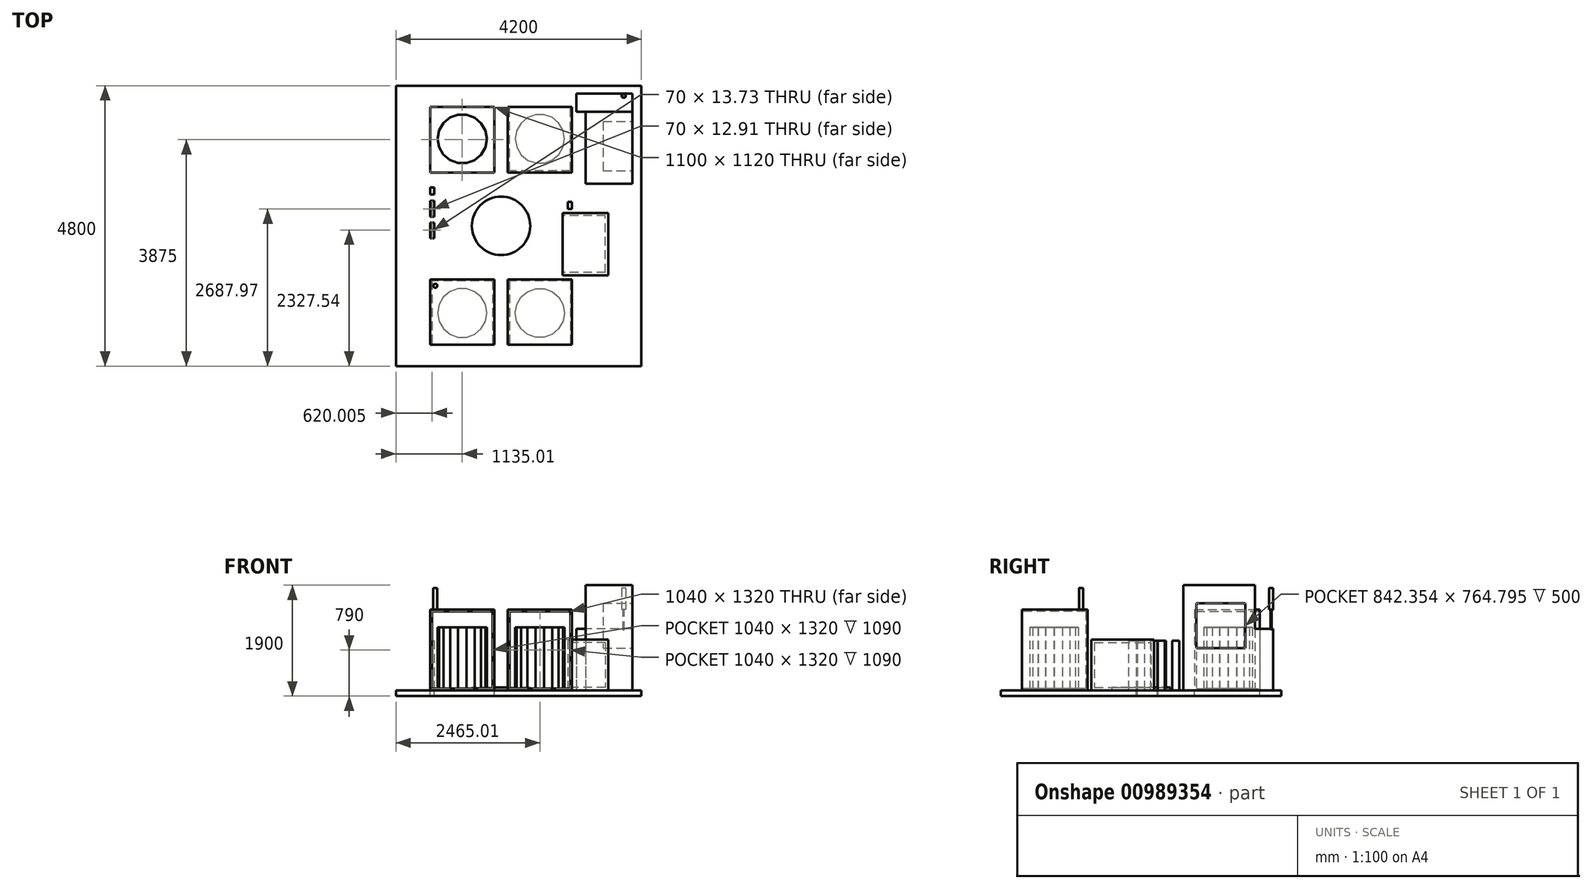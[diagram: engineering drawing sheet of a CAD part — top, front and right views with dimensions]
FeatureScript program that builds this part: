
annotation { "Feature Type Name" : "Feature", "Feature Type Description" : "" }
export const myFeature = defineFeature(function(context is Context, id is Id, definition is map)
    precondition{}
    {
        {
            var Q0;
            Q0=qCreatedBy(makeId("Top.planeOp"),FACE);
            var sketch = newSketch(context, id + "F0", { "sketchPlane" : qUnion([Q0])});
            skLineSegment(sketch, "E0.bottom", {"start": v(-4186.95, 4400.9) * mm, "end": v(13.05, 4400.9) * mm});
            skLineSegment(sketch, "E0.top", {"start": v(-4186.95, -399.1) * mm, "end": v(13.05, -399.1) * mm});
            skLineSegment(sketch, "E0.left", {"start": v(-4186.95, 4400.9) * mm, "end": v(-4186.95, -399.1) * mm});
            skLineSegment(sketch, "E0.right", {"start": v(13.05, 4400.9) * mm, "end": v(13.05, -399.1) * mm});
            skLineSegment(sketch, "E1", {"start": v(13.05, 2000.9) * mm, "end": v(-2386.95, 2000.9) * mm});
            skCircle(sketch, "E2", {"center": v(-2386.95, 2000.9) * mm, "radius": 500 * mm});
            skLineSegment(sketch, "E3.bottom", {"start": v(-2504.03, 4400.9) * mm, "end": v(-3604.03, 4400.9) * mm});
            skLineSegment(sketch, "E4.bottom", {"start": v(-1092.36, 4400.9) * mm, "end": v(-2192.36, 4400.9) * mm});
            skLineSegment(sketch, "E5.bottom", {"start": v(-550.98, 1154) * mm, "end": v(-1330.98, 1154) * mm});
            skLineSegment(sketch, "E5.top", {"start": v(-550.98, 2224) * mm, "end": v(-1330.98, 2224) * mm});
            skLineSegment(sketch, "E5.left", {"start": v(-550.98, 1154) * mm, "end": v(-550.98, 2224) * mm});
            skLineSegment(sketch, "E5.right", {"start": v(-1330.98, 1154) * mm, "end": v(-1330.98, 2224) * mm});
            skLineSegment(sketch, "E6.bottom", {"start": v(-141.16, 2724.16) * mm, "end": v(-941.16, 2724.16) * mm});
            skLineSegment(sketch, "E6.top", {"start": v(-141.16, 3954.16) * mm, "end": v(-941.16, 3954.16) * mm});
            skLineSegment(sketch, "E6.left", {"start": v(-141.16, 2724.16) * mm, "end": v(-141.16, 3954.16) * mm});
            skLineSegment(sketch, "E6.right", {"start": v(-941.16, 2724.16) * mm, "end": v(-941.16, 3954.16) * mm});
            skLineSegment(sketch, "E7.bottom", {"start": v(-141.16, 3954.16) * mm, "end": v(-1101.16, 3954.16) * mm});
            skLineSegment(sketch, "E7.top", {"start": v(-141.16, 4264.16) * mm, "end": v(-1101.16, 4264.16) * mm});
            skLineSegment(sketch, "E7.left", {"start": v(-141.16, 3954.16) * mm, "end": v(-141.16, 4264.16) * mm});
            skLineSegment(sketch, "E7.right", {"start": v(-1101.16, 3954.16) * mm, "end": v(-1101.16, 4264.16) * mm});
            skLineSegment(sketch, "E8.bottom", {"start": v(-1171.95, 1085.9) * mm, "end": v(-3601.95, 1085.9) * mm});
            skLineSegment(sketch, "E8.top", {"start": v(-1171.95, 2915.9) * mm, "end": v(-3601.95, 2915.9) * mm});
            skLineSegment(sketch, "E8.left", {"start": v(-1171.95, 1085.9) * mm, "end": v(-1171.95, 2915.9) * mm});
            skLineSegment(sketch, "E8.right", {"start": v(-3601.95, 1085.9) * mm, "end": v(-3601.95, 2915.9) * mm});
            skLineSegment(sketch, "E9.bottom", {"start": v(-1171.95, 2915.9) * mm, "end": v(-2271.95, 2915.9) * mm});
            skLineSegment(sketch, "E9.top", {"start": v(-1171.95, 4035.9) * mm, "end": v(-2271.95, 4035.9) * mm});
            skLineSegment(sketch, "E9.left", {"start": v(-1171.95, 2915.9) * mm, "end": v(-1171.95, 4035.9) * mm});
            skLineSegment(sketch, "E9.right", {"start": v(-2271.95, 2915.9) * mm, "end": v(-2271.95, 4035.9) * mm});
            skLineSegment(sketch, "E10.bottom", {"start": v(-3601.95, 2915.9) * mm, "end": v(-2501.95, 2915.9) * mm});
            skLineSegment(sketch, "E10.top", {"start": v(-3601.95, 4035.9) * mm, "end": v(-2501.95, 4035.9) * mm});
            skLineSegment(sketch, "E10.left", {"start": v(-3601.95, 2915.9) * mm, "end": v(-3601.95, 4035.9) * mm});
            skLineSegment(sketch, "E10.right", {"start": v(-2501.95, 2915.9) * mm, "end": v(-2501.95, 4035.9) * mm});
            skLineSegment(sketch, "E11.MirrorCS", {"start": v(-1171.95, 1085.9) * mm, "end": v(-1171.95, -34.1) * mm});
            skLineSegment(sketch, "E12.MirrorCS", {"start": v(-1171.95, -34.1) * mm, "end": v(-2271.95, -34.1) * mm});
            skLineSegment(sketch, "E13.MirrorCS", {"start": v(-2271.95, 1085.9) * mm, "end": v(-2271.95, -34.1) * mm});
            skLineSegment(sketch, "E14.MirrorCS", {"start": v(-2501.95, 1085.9) * mm, "end": v(-2501.95, -34.1) * mm});
            skLineSegment(sketch, "E15.MirrorCS", {"start": v(-3601.95, -34.1) * mm, "end": v(-2501.95, -34.1) * mm});
            skLineSegment(sketch, "E16.MirrorCS", {"start": v(-3601.95, 1085.9) * mm, "end": v(-3601.95, -34.1) * mm});
            skLineSegment(sketch, "E17.bottom", {"start": v(-1171.95, 2408.86) * mm, "end": v(-1241.95, 2408.86) * mm});
            skLineSegment(sketch, "E17.top", {"start": v(-1171.95, 2288.86) * mm, "end": v(-1241.95, 2288.86) * mm});
            skLineSegment(sketch, "E17.left", {"start": v(-1171.95, 2408.86) * mm, "end": v(-1171.95, 2288.86) * mm});
            skLineSegment(sketch, "E17.right", {"start": v(-1241.95, 2408.86) * mm, "end": v(-1241.95, 2288.86) * mm});
            skLineSegment(sketch, "E18.left", {"start": v(-3601.95, 2000.9) * mm, "end": v(-3601.95, 2383.24) * mm});
            skLineSegment(sketch, "E19.bottom", {"start": v(-3601.95, 1786.57) * mm, "end": v(-3531.95, 1786.57) * mm});
            skLineSegment(sketch, "E19.top", {"start": v(-3601.95, 2056.57) * mm, "end": v(-3531.95, 2056.57) * mm});
            skLineSegment(sketch, "E19.left", {"start": v(-3601.95, 1786.57) * mm, "end": v(-3601.95, 2056.57) * mm});
            skLineSegment(sketch, "E19.right", {"start": v(-3531.95, 1786.57) * mm, "end": v(-3531.95, 2056.57) * mm});
            skLineSegment(sketch, "E20.bottom", {"start": v(-3601.95, 2160.32) * mm, "end": v(-3531.95, 2160.32) * mm});
            skLineSegment(sketch, "E20.top", {"start": v(-3601.95, 2430.32) * mm, "end": v(-3531.95, 2430.32) * mm});
            skLineSegment(sketch, "E20.left", {"start": v(-3601.95, 2160.32) * mm, "end": v(-3601.95, 2430.32) * mm});
            skLineSegment(sketch, "E20.right", {"start": v(-3531.95, 2160.32) * mm, "end": v(-3531.95, 2430.32) * mm});
            skLineSegment(sketch, "E21.bottom", {"start": v(-3601.95, 2538.18) * mm, "end": v(-3531.95, 2538.18) * mm});
            skLineSegment(sketch, "E21.top", {"start": v(-3601.95, 2658.18) * mm, "end": v(-3531.95, 2658.18) * mm});
            skLineSegment(sketch, "E21.left", {"start": v(-3601.95, 2538.18) * mm, "end": v(-3601.95, 2658.18) * mm});
            skLineSegment(sketch, "E21.right", {"start": v(-3531.95, 2538.18) * mm, "end": v(-3531.95, 2658.18) * mm});
            skLineSegment(sketch, "E22", {"start": v(-3531.95, 2295.32) * mm, "end": v(-3601.95, 2295.32) * mm});
            skLineSegment(sketch, "E23", {"start": v(-3531.95, 1921.57) * mm, "end": v(-3601.95, 1921.57) * mm});
            skLineSegment(sketch, "E24", {"start": v(-3531.95, 2282.4) * mm, "end": v(-3601.95, 2282.4) * mm});
            skLineSegment(sketch, "E25", {"start": v(-3531.95, 1933.96) * mm, "end": v(-3601.95, 1935.3) * mm});
            skLineSegment(sketch, "E26", {"start": v(-1171.95, 2915.9) * mm, "end": v(-2386.95, 2915.9) * mm});
            skLineSegment(sketch, "E27", {"start": v(-2386.95, 2915.9) * mm, "end": v(-2386.95, 4048.28) * mm});
            skSolve(sketch);
        }
        {
            var Q0;
            Q0=makeQuery(id+"F0.imprint","IMPRINT",FACE,{"disambiguationData":[TD([[makeQuery(id+"F0.imprint","IMPRINT",EDGE,{"derivedFrom":sQuery(id+"F0.wireOp",EDGE,"E9.bottom")}),-1.0]])]});
            var Q1;
            Q1=makeQuery(id+"F0.imprint","IMPRINT",FACE,{"disambiguationData":[TD([[makeQuery(id+"F0.imprint","IMPRINT",EDGE,{"derivedFrom":sQuery(id+"F0.wireOp",EDGE,"E10.bottom")}),1.0]])]});
            var Q2;
            {var subQ0=sQuery(id+"F0.wireOp",EDGE,"E11.MirrorCS");Q2=makeQuery(id+"F0.imprint","IMPRINT",FACE,{"disambiguationData":[TD([[makeQuery(id+"F0.imprint","IMPRINT",EDGE,{"derivedFrom":subQ0}),-1.0]])]});}
            var Q3;
            {var subQ2=sQuery(id+"F0.wireOp",EDGE,"E14.MirrorCS");Q3=makeQuery(id+"F0.imprint","IMPRINT",FACE,{"disambiguationData":[TD([[makeQuery(id+"F0.imprint","IMPRINT",EDGE,{"derivedFrom":subQ2}),-1.0]])]});}
            var Q4;
            Q4=makeQuery(id+"F0.imprint","IMPRINT",FACE,{"disambiguationData":[TD([[makeQuery(id+"F0.imprint","IMPRINT",EDGE,{"derivedFrom":sQuery(id+"F0.wireOp",EDGE,"E9.top")}),1.0]])]});
            extrude(context, id + "F1", {"entities" : qUnion([Q0, Q1, Q2, Q3, Q4]), "depth" : 1380 * mm, "offsetDistance" : 25 * mm});
        }
        {
            var Q0;
            Q0=makeQuery(id+"F0.imprint","IMPRINT",FACE,{"disambiguationData":[TD([[makeQuery(id+"F0.imprint","IMPRINT",EDGE,{"derivedFrom":sQuery(id+"F0.wireOp",EDGE,"E6.bottom")}),-1.0]])]});
            extrude(context, id + "F2", {"entities" : qUnion([Q0]), "depth" : 1800 * mm, "offsetDistance" : 25 * mm});
        }
        {
            var Q0;
            Q0=makeQuery(id+"F0.imprint","IMPRINT",FACE,{"disambiguationData":[TD([[makeQuery(id+"F0.imprint","IMPRINT",EDGE,{"derivedFrom":sQuery(id+"F0.wireOp",EDGE,"E7.top")}),1.0]])]});
            extrude(context, id + "F3", {"entities" : qUnion([Q0]), "operationType" : NewBodyOperationType.ADD, "depth" : 1050 * mm, "offsetDistance" : 25 * mm});
        }
        {
            var Q0;
            Q0=makeQuery(id+"F0.imprint","IMPRINT",FACE,{"disambiguationData":[TD([[makeQuery(id+"F0.imprint","IMPRINT",EDGE,{"derivedFrom":sQuery(id+"F0.wireOp",EDGE,"E21.bottom")}),1.0]])]});
            var Q1;
            {var subQ1=sQuery(id+"F0.wireOp",EDGE,"E20.top");Q1=makeQuery(id+"F0.imprint","IMPRINT",FACE,{"disambiguationData":[TD([[makeQuery(id+"F0.imprint","IMPRINT",EDGE,{"derivedFrom":subQ1}),-1.0]])]});}
            var Q2;
            {var subQ0=sQuery(id+"F0.wireOp",EDGE,"E20.bottom");Q2=makeQuery(id+"F0.imprint","IMPRINT",FACE,{"disambiguationData":[TD([[makeQuery(id+"F0.imprint","IMPRINT",EDGE,{"derivedFrom":subQ0}),1.0]])]});}
            var Q3;
            {var subQ1=sQuery(id+"F0.wireOp",EDGE,"E19.top");Q3=makeQuery(id+"F0.imprint","IMPRINT",FACE,{"disambiguationData":[TD([[makeQuery(id+"F0.imprint","IMPRINT",EDGE,{"derivedFrom":subQ1}),-1.0]])]});}
            var Q4;
            {var subQ0=sQuery(id+"F0.wireOp",EDGE,"E19.bottom");Q4=makeQuery(id+"F0.imprint","IMPRINT",FACE,{"disambiguationData":[TD([[makeQuery(id+"F0.imprint","IMPRINT",EDGE,{"derivedFrom":subQ0}),1.0]])]});}
            var Q5;
            Q5=makeQuery(id+"F0.imprint","IMPRINT",FACE,{"disambiguationData":[TD([[makeQuery(id+"F0.imprint","IMPRINT",EDGE,{"derivedFrom":sQuery(id+"F0.wireOp",EDGE,"E17.bottom")}),1.0]])]});
            extrude(context, id + "F4", {"entities" : qUnion([Q0, Q1, Q2, Q3, Q4, Q5]), "depth" : 850 * mm, "offsetDistance" : 25 * mm});
        }
        {
            var Q0;
            Q0=makeQuery(id+"F1.opExtrude","SWEPT_FACE",FACE,{"disambiguationData":[OSD([sQuery(id+"F0.wireOp",EDGE,"E12.MirrorCS")])]});
            var Q1;
            Q1=makeQuery(id+"F1.opExtrude","SWEPT_FACE",FACE,{"disambiguationData":[OSD([sQuery(id+"F0.wireOp",EDGE,"E15.MirrorCS")])]});
            var Q2;
            Q2=makeQuery(id+"F1.opExtrude","SWEPT_FACE",FACE,{"disambiguationData":[OSD([sQuery(id+"F0.wireOp",EDGE,"E10.top")])]});
            var Q3;
            Q3=makeQuery(id+"F1.opExtrude","SWEPT_FACE",FACE,{"disambiguationData":[OSD([sQuery(id+"F0.wireOp",EDGE,"E9.top")])]});
            shell(context, id + "F5", {"entities" : qUnion([Q0, Q1, Q2, Q3]), "thickness" : 30 * mm});
        }
        {
            var Q0;
            Q0=makeQuery(id+"F5.opShell","OFFSET_FACE",FACE,{"disambiguationData":[OSD([sQuery(id+"F0.wireOp",EDGE,"E8.bottom"),sQuery(id+"F0.wireOp",EDGE,"E11.MirrorCS"),sQuery(id+"F0.wireOp",EDGE,"E12.MirrorCS"),sQuery(id+"F0.wireOp",EDGE,"E13.MirrorCS")])]});
            var sketch = newSketch(context, id + "F6", { "sketchPlane" : qUnion([Q0])});
            skLineSegment(sketch, "E28.bottom", {"start": v(-2241.95, -34.1) * mm, "end": v(-1201.95, -34.1) * mm});
            skLineSegment(sketch, "E28.top", {"start": v(-2241.95, 1055.9) * mm, "end": v(-1201.95, 1055.9) * mm});
            skLineSegment(sketch, "E28.left", {"start": v(-2241.95, -34.1) * mm, "end": v(-2241.95, 1055.9) * mm});
            skLineSegment(sketch, "E28.right", {"start": v(-1201.95, -34.1) * mm, "end": v(-1201.95, 1055.9) * mm});
            skLineSegment(sketch, "E29", {"start": v(-1721.95, -34.1) * mm, "end": v(-1721.95, 1055.9) * mm});
            skLineSegment(sketch, "E30", {"start": v(-1721.95, 1055.9) * mm, "end": v(-1721.95, 510.9) * mm});
            skLineSegment(sketch, "E31", {"start": v(-1721.95, 510.9) * mm, "end": v(-1201.95, 510.9) * mm});
            skLineSegment(sketch, "E32", {"start": v(-1201.95, 510.9) * mm, "end": v(-2241.95, 510.9) * mm});
            skCircle(sketch, "E33.cCircle", {"center": v(-1721.95, 510.9) * mm, "radius": 415.23 * mm, "construction": true});
            skLineSegment(sketch, "E33.0", {"start": v(-2043.51, 783.6) * mm, "end": v(-1930.85, 877.14) * mm});
            skLineSegment(sketch, "E33.1", {"start": v(-1930.85, 877.14) * mm, "end": v(-1792.99, 926.5) * mm});
            skLineSegment(sketch, "E33.2", {"start": v(-1792.99, 926.5) * mm, "end": v(-1646.56, 925.73) * mm});
            skLineSegment(sketch, "E33.3", {"start": v(-1646.56, 925.73) * mm, "end": v(-1509.22, 874.93) * mm});
            skLineSegment(sketch, "E33.4", {"start": v(-1509.22, 874.93) * mm, "end": v(-1397.54, 780.22) * mm});
            skLineSegment(sketch, "E33.5", {"start": v(-1397.54, 780.22) * mm, "end": v(-1324.99, 653.03) * mm});
            skLineSegment(sketch, "E33.6", {"start": v(-1324.99, 653.03) * mm, "end": v(-1300.32, 508.69) * mm});
            skLineSegment(sketch, "E33.7", {"start": v(-1300.32, 508.69) * mm, "end": v(-1326.5, 364.62) * mm});
            skLineSegment(sketch, "E33.8", {"start": v(-1326.5, 364.62) * mm, "end": v(-1400.38, 238.19) * mm});
            skLineSegment(sketch, "E33.9", {"start": v(-1400.38, 238.19) * mm, "end": v(-1513.04, 144.65) * mm});
            skLineSegment(sketch, "E33.10", {"start": v(-1513.04, 144.65) * mm, "end": v(-1650.9, 95.29) * mm});
            skLineSegment(sketch, "E33.11", {"start": v(-1650.9, 95.29) * mm, "end": v(-1797.33, 96.05) * mm});
            skLineSegment(sketch, "E33.12", {"start": v(-1797.33, 96.05) * mm, "end": v(-1934.67, 146.86) * mm});
            skLineSegment(sketch, "E33.13", {"start": v(-1934.67, 146.86) * mm, "end": v(-2046.35, 241.57) * mm});
            skLineSegment(sketch, "E33.14", {"start": v(-2046.35, 241.57) * mm, "end": v(-2118.9, 368.76) * mm});
            skLineSegment(sketch, "E33.15", {"start": v(-2118.9, 368.76) * mm, "end": v(-2143.57, 513.1) * mm});
            skLineSegment(sketch, "E33.16", {"start": v(-2143.57, 513.1) * mm, "end": v(-2117.4, 657.17) * mm});
            skLineSegment(sketch, "E33.17", {"start": v(-2117.4, 657.17) * mm, "end": v(-2043.51, 783.6) * mm});
            skPoint(sketch, "E33.0.midPoint", {"position": v(-1987.18, 830.37) * mm});
            skLineSegment(sketch, "E34.MirrorCS", {"start": v(-1721.95, 4035.9) * mm, "end": v(-1721.95, 2945.9) * mm});
            skLineSegment(sketch, "E35.MirrorCS", {"start": v(-1201.95, 3490.9) * mm, "end": v(-2241.95, 3490.9) * mm});
            skLineSegment(sketch, "E36.MirrorCS", {"start": v(-2117.4, 3344.62) * mm, "end": v(-2043.51, 3218.19) * mm});
            skLineSegment(sketch, "E37.MirrorCS", {"start": v(-1650.9, 3906.5) * mm, "end": v(-1797.33, 3905.73) * mm});
            skLineSegment(sketch, "E38.MirrorCS", {"start": v(-2043.51, 3218.19) * mm, "end": v(-1930.85, 3124.65) * mm});
            skLineSegment(sketch, "E39.MirrorCS", {"start": v(-1326.5, 3637.17) * mm, "end": v(-1400.38, 3763.6) * mm});
            skLineSegment(sketch, "E40.MirrorCS", {"start": v(-1513.04, 3857.14) * mm, "end": v(-1650.9, 3906.5) * mm});
            skLineSegment(sketch, "E41.MirrorCS", {"start": v(-1397.54, 3221.57) * mm, "end": v(-1324.99, 3348.76) * mm});
            skLineSegment(sketch, "E42.MirrorCS", {"start": v(-2118.9, 3633.03) * mm, "end": v(-2143.57, 3488.69) * mm});
            skLineSegment(sketch, "E43.MirrorCS", {"start": v(-1797.33, 3905.73) * mm, "end": v(-1934.67, 3854.93) * mm});
            skLineSegment(sketch, "E44.MirrorCS", {"start": v(-1930.85, 3124.65) * mm, "end": v(-1792.99, 3075.29) * mm});
            skLineSegment(sketch, "E45.MirrorCS", {"start": v(-1646.56, 3076.05) * mm, "end": v(-1509.22, 3126.86) * mm});
            skLineSegment(sketch, "E46.MirrorCS", {"start": v(-2046.35, 3760.22) * mm, "end": v(-2118.9, 3633.03) * mm});
            skLineSegment(sketch, "E47.MirrorCS", {"start": v(-1509.22, 3126.86) * mm, "end": v(-1397.54, 3221.57) * mm});
            skLineSegment(sketch, "E48.MirrorCS", {"start": v(-1934.67, 3854.93) * mm, "end": v(-2046.35, 3760.22) * mm});
            skLineSegment(sketch, "E49.MirrorCS", {"start": v(-2143.57, 3488.69) * mm, "end": v(-2117.4, 3344.62) * mm});
            skCircle(sketch, "E50.MirrorC", {"center": v(-1721.95, 3490.9) * mm, "radius": 415.23 * mm, "construction": true});
            skLineSegment(sketch, "E51.MirrorCS", {"start": v(-1400.38, 3763.6) * mm, "end": v(-1513.04, 3857.14) * mm});
            skLineSegment(sketch, "E52.MirrorCS", {"start": v(-1300.32, 3493.1) * mm, "end": v(-1326.5, 3637.17) * mm});
            skLineSegment(sketch, "E53.MirrorCS", {"start": v(-1324.99, 3348.76) * mm, "end": v(-1300.32, 3493.1) * mm});
            skLineSegment(sketch, "E54.MirrorCS", {"start": v(-1792.99, 3075.29) * mm, "end": v(-1646.56, 3076.05) * mm});
            skLineSegment(sketch, "E55.MirrorCS", {"start": v(-1721.95, 3490.9) * mm, "end": v(-1201.95, 3490.9) * mm});
            skPoint(sketch, "E56.MirrorP", {"position": v(-1987.18, 3171.42) * mm});
            skLineSegment(sketch, "E57.MirrorCS", {"start": v(-1721.95, 2945.9) * mm, "end": v(-1721.95, 3490.9) * mm});
            skLineSegment(sketch, "E58.MirrorCS", {"start": v(-2976.56, 3905.73) * mm, "end": v(-2839.22, 3854.93) * mm});
            skLineSegment(sketch, "E59.MirrorCS", {"start": v(-2839.22, 3854.93) * mm, "end": v(-2727.54, 3760.22) * mm});
            skLineSegment(sketch, "E60.MirrorCS", {"start": v(-2727.54, 3760.22) * mm, "end": v(-2654.99, 3633.03) * mm});
            skLineSegment(sketch, "E61.MirrorCS", {"start": v(-2656.5, 3344.62) * mm, "end": v(-2730.38, 3218.19) * mm});
            skLineSegment(sketch, "E62.MirrorCS", {"start": v(-3127.33, 3076.05) * mm, "end": v(-3264.67, 3126.86) * mm});
            skLineSegment(sketch, "E63.MirrorCS", {"start": v(-3264.67, 3126.86) * mm, "end": v(-3376.35, 3221.57) * mm});
            skCircle(sketch, "E64.MirrorC", {"center": v(-3051.95, 3490.9) * mm, "radius": 415.23 * mm, "construction": true});
            skLineSegment(sketch, "E65.MirrorCS", {"start": v(-3373.51, 3763.6) * mm, "end": v(-3260.85, 3857.14) * mm});
            skLineSegment(sketch, "E66.MirrorCS", {"start": v(-2630.32, 3488.69) * mm, "end": v(-2656.5, 3344.62) * mm});
            skLineSegment(sketch, "E67.MirrorCS", {"start": v(-3447.4, 3637.17) * mm, "end": v(-3373.51, 3763.6) * mm});
            skLineSegment(sketch, "E68.MirrorCS", {"start": v(-2730.38, 3218.19) * mm, "end": v(-2843.04, 3124.65) * mm});
            skLineSegment(sketch, "E69.MirrorCS", {"start": v(-3260.85, 3857.14) * mm, "end": v(-3122.99, 3906.5) * mm});
            skLineSegment(sketch, "E70.MirrorCS", {"start": v(-3376.35, 3221.57) * mm, "end": v(-3448.9, 3348.76) * mm});
            skLineSegment(sketch, "E71.MirrorCS", {"start": v(-3448.9, 3348.76) * mm, "end": v(-3473.57, 3493.1) * mm});
            skLineSegment(sketch, "E72.MirrorCS", {"start": v(-3473.57, 3493.1) * mm, "end": v(-3447.4, 3637.17) * mm});
            skLineSegment(sketch, "E73.MirrorCS", {"start": v(-2654.99, 3633.03) * mm, "end": v(-2630.32, 3488.69) * mm});
            skLineSegment(sketch, "E74.MirrorCS", {"start": v(-3122.99, 3906.5) * mm, "end": v(-2976.56, 3905.73) * mm});
            skLineSegment(sketch, "E75.MirrorCS", {"start": v(-2980.9, 3075.29) * mm, "end": v(-3127.33, 3076.05) * mm});
            skLineSegment(sketch, "E76.MirrorCS", {"start": v(-2843.04, 3124.65) * mm, "end": v(-2980.9, 3075.29) * mm});
            skLineSegment(sketch, "E77.MirrorCS", {"start": v(-3051.95, 3490.9) * mm, "end": v(-3571.95, 3490.9) * mm});
            skLineSegment(sketch, "E78.MirrorCS", {"start": v(-3571.95, 3490.9) * mm, "end": v(-2531.95, 3490.9) * mm});
            skLineSegment(sketch, "E79.MirrorCS", {"start": v(-3051.95, 4035.9) * mm, "end": v(-3051.95, 2945.9) * mm});
            skLineSegment(sketch, "E80.MirrorCS", {"start": v(-3051.95, 2945.9) * mm, "end": v(-3051.95, 3490.9) * mm});
            skPoint(sketch, "E81.MirrorP", {"position": v(-2786.7, 3171.42) * mm});
            skLineSegment(sketch, "E82.MirrorCS", {"start": v(-2839.22, 146.86) * mm, "end": v(-2727.54, 241.57) * mm});
            skLineSegment(sketch, "E83.MirrorCS", {"start": v(-2727.54, 241.57) * mm, "end": v(-2654.99, 368.76) * mm});
            skLineSegment(sketch, "E84.MirrorCS", {"start": v(-2976.56, 96.05) * mm, "end": v(-2839.22, 146.86) * mm});
            skLineSegment(sketch, "E85.MirrorCS", {"start": v(-2630.32, 513.1) * mm, "end": v(-2656.5, 657.17) * mm});
            skLineSegment(sketch, "E86.MirrorCS", {"start": v(-3122.99, 95.29) * mm, "end": v(-2976.56, 96.05) * mm});
            skLineSegment(sketch, "E87.MirrorCS", {"start": v(-3373.51, 238.19) * mm, "end": v(-3260.85, 144.65) * mm});
            skLineSegment(sketch, "E88.MirrorCS", {"start": v(-3260.85, 144.65) * mm, "end": v(-3122.99, 95.29) * mm});
            skLineSegment(sketch, "E89.MirrorCS", {"start": v(-2843.04, 877.14) * mm, "end": v(-2980.9, 926.5) * mm});
            skLineSegment(sketch, "E90.MirrorCS", {"start": v(-3127.33, 925.73) * mm, "end": v(-3264.67, 874.93) * mm});
            skLineSegment(sketch, "E91.MirrorCS", {"start": v(-2656.5, 657.17) * mm, "end": v(-2730.38, 783.6) * mm});
            skLineSegment(sketch, "E92.MirrorCS", {"start": v(-3448.9, 653.03) * mm, "end": v(-3473.57, 508.69) * mm});
            skLineSegment(sketch, "E93.MirrorCS", {"start": v(-2654.99, 368.76) * mm, "end": v(-2630.32, 513.1) * mm});
            skCircle(sketch, "E94.MirrorC", {"center": v(-3051.95, 510.9) * mm, "radius": 415.23 * mm, "construction": true});
            skLineSegment(sketch, "E95.MirrorCS", {"start": v(-3473.57, 508.69) * mm, "end": v(-3447.4, 364.62) * mm});
            skLineSegment(sketch, "E96.MirrorCS", {"start": v(-3447.4, 364.62) * mm, "end": v(-3373.51, 238.19) * mm});
            skLineSegment(sketch, "E97.MirrorCS", {"start": v(-2980.9, 926.5) * mm, "end": v(-3127.33, 925.73) * mm});
            skLineSegment(sketch, "E98.MirrorCS", {"start": v(-3264.67, 874.93) * mm, "end": v(-3376.35, 780.22) * mm});
            skLineSegment(sketch, "E99.MirrorCS", {"start": v(-3376.35, 780.22) * mm, "end": v(-3448.9, 653.03) * mm});
            skLineSegment(sketch, "E100.MirrorCS", {"start": v(-2730.38, 783.6) * mm, "end": v(-2843.04, 877.14) * mm});
            skPoint(sketch, "E101.MirrorP", {"position": v(-2786.7, 830.37) * mm});
            skSolve(sketch);
        }
        {
            var Q0;
            {var subQ0=sQuery(id+"F6.wireOp",EDGE,"E33.7");Q0=makeQuery(id+"F6.imprint","IMPRINT",FACE,{"disambiguationData":[TD([[makeQuery(id+"F6.imprint","IMPRINT",EDGE,{"derivedFrom":subQ0}),-1.0]])]});}
            var Q1;
            {var subQ0=sQuery(id+"F6.wireOp",EDGE,"E33.12");Q1=makeQuery(id+"F6.imprint","IMPRINT",FACE,{"disambiguationData":[TD([[makeQuery(id+"F6.imprint","IMPRINT",EDGE,{"derivedFrom":subQ0}),-1.0]])]});}
            var Q2;
            Q2=makeQuery(id+"F6.imprint","IMPRINT",FACE,{"disambiguationData":[TD([[makeQuery(id+"F6.imprint","IMPRINT",EDGE,{"derivedFrom":sQuery(id+"F6.wireOp",EDGE,"E33.0")}),-1.0]])]});
            var Q3;
            {var subQ0=sQuery(id+"F6.wireOp",EDGE,"E33.3");Q3=makeQuery(id+"F6.imprint","IMPRINT",FACE,{"disambiguationData":[TD([[makeQuery(id+"F6.imprint","IMPRINT",EDGE,{"derivedFrom":subQ0}),-1.0]])]});}
            var Q4;
            Q4=makeQuery(id+"F6.imprint","IMPRINT",FACE,{"disambiguationData":[TD([[makeQuery(id+"F6.imprint","IMPRINT",EDGE,{"derivedFrom":sQuery(id+"F6.wireOp",EDGE,"E36.MirrorCS")}),1.0]])]});
            var Q5;
            {var subQ1=sQuery(id+"F6.wireOp",EDGE,"E41.MirrorCS");Q5=makeQuery(id+"F6.imprint","IMPRINT",FACE,{"disambiguationData":[TD([[makeQuery(id+"F6.imprint","IMPRINT",EDGE,{"derivedFrom":subQ1}),1.0]])]});}
            var Q6;
            Q6=makeQuery(id+"F6.imprint","IMPRINT",FACE,{"disambiguationData":[TD([[makeQuery(id+"F6.imprint","IMPRINT",EDGE,{"derivedFrom":sQuery(id+"F6.wireOp",EDGE,"E39.MirrorCS")}),1.0]])]});
            var Q7;
            {var subQ8=sQuery(id+"F6.wireOp",EDGE,"E43.MirrorCS");Q7=makeQuery(id+"F6.imprint","IMPRINT",FACE,{"disambiguationData":[TD([[makeQuery(id+"F6.imprint","IMPRINT",EDGE,{"derivedFrom":subQ8}),1.0]])]});}
            var Q8;
            {var subQ8=sQuery(id+"F6.wireOp",EDGE,"E58.MirrorCS");Q8=makeQuery(id+"F6.imprint","IMPRINT",FACE,{"disambiguationData":[TD([[makeQuery(id+"F6.imprint","IMPRINT",EDGE,{"derivedFrom":subQ8}),-1.0]])]});}
            var Q9;
            Q9=makeQuery(id+"F6.imprint","IMPRINT",FACE,{"disambiguationData":[TD([[makeQuery(id+"F6.imprint","IMPRINT",EDGE,{"derivedFrom":sQuery(id+"F6.wireOp",EDGE,"E61.MirrorCS")}),-1.0]])]});
            var Q10;
            {var subQ6=sQuery(id+"F6.wireOp",EDGE,"E62.MirrorCS");Q10=makeQuery(id+"F6.imprint","IMPRINT",FACE,{"disambiguationData":[TD([[makeQuery(id+"F6.imprint","IMPRINT",EDGE,{"derivedFrom":subQ6}),-1.0]])]});}
            var Q11;
            Q11=makeQuery(id+"F6.imprint","IMPRINT",FACE,{"disambiguationData":[TD([[makeQuery(id+"F6.imprint","IMPRINT",EDGE,{"derivedFrom":sQuery(id+"F6.wireOp",EDGE,"E65.MirrorCS")}),-1.0]])]});
            var Q12;
            Q12=makeQuery(id+"F6.imprint","IMPRINT",FACE,{"disambiguationData":[TD([[makeQuery(id+"F6.imprint","IMPRINT",EDGE,{"derivedFrom":sQuery(id+"F6.wireOp",EDGE,"E82.MirrorCS")}),1.0]])]});
            extrude(context, id + "F7", {"entities" : qUnion([Q0, Q1, Q2, Q3, Q4, Q5, Q6, Q7, Q8, Q9, Q10, Q11, Q12]), "operationType" : NewBodyOperationType.ADD, "depth" : 1050 * mm, "offsetDistance" : 25 * mm});
        }
        {
            var Q0;
            {var subQ0=sQuery(id+"F0.wireOp",EDGE,"E5.left");var subQ1=sQuery(id+"F0.wireOp",EDGE,"E1");var subQ2=makeQuery(id+"F0.imprint","INTERSECT",VERTEX,{"derivedFrom":[subQ1,subQ0]});Q0=makeQuery(id+"F0.imprint","IMPRINT",FACE,{"disambiguationData":[TD([[makeQuery(id+"F0.imprint","IMPRINT",EDGE,{"disambiguationData":[TD([[subQ2,-1.0]])],"derivedFrom":subQ1}),-1.0]])]});}
            var Q1;
            {var subQ0=sQuery(id+"F0.wireOp",EDGE,"E5.left");var subQ1=sQuery(id+"F0.wireOp",EDGE,"E1");var subQ2=makeQuery(id+"F0.imprint","INTERSECT",VERTEX,{"derivedFrom":[subQ1,subQ0]});Q1=makeQuery(id+"F0.imprint","IMPRINT",FACE,{"disambiguationData":[TD([[makeQuery(id+"F0.imprint","IMPRINT",EDGE,{"disambiguationData":[TD([[subQ2,-1.0]])],"derivedFrom":subQ1}),1.0]])]});}
            var Q2;
            {var subQ0=sQuery(id+"F0.wireOp",EDGE,"E5.right");var subQ1=sQuery(id+"F0.wireOp",EDGE,"E1");var subQ2=makeQuery(id+"F0.imprint","INTERSECT",VERTEX,{"derivedFrom":[subQ1,subQ0]});Q2=makeQuery(id+"F0.imprint","IMPRINT",FACE,{"disambiguationData":[TD([[makeQuery(id+"F0.imprint","IMPRINT",EDGE,{"disambiguationData":[TD([[subQ2,1.0]])],"derivedFrom":subQ1}),1.0]])]});}
            var Q3;
            {var subQ0=sQuery(id+"F0.wireOp",EDGE,"E5.right");var subQ1=sQuery(id+"F0.wireOp",EDGE,"E1");var subQ2=makeQuery(id+"F0.imprint","INTERSECT",VERTEX,{"derivedFrom":[subQ1,subQ0]});Q3=makeQuery(id+"F0.imprint","IMPRINT",FACE,{"disambiguationData":[TD([[makeQuery(id+"F0.imprint","IMPRINT",EDGE,{"disambiguationData":[TD([[subQ2,1.0]])],"derivedFrom":subQ1}),-1.0]])]});}
            extrude(context, id + "F8", {"entities" : qUnion([Q0, Q1, Q2, Q3]), "depth" : 870 * mm, "offsetDistance" : 25 * mm});
        }
        {
            var Q0;
            Q0=makeQuery(id+"F8.opExtrude","SWEPT_FACE",FACE,{"disambiguationData":[OSD([sQuery(id+"F0.wireOp",EDGE,"E5.right")])]});
            shell(context, id + "F9", {"entities" : qUnion([Q0]), "thickness" : 50 * mm});
        }
        {
            var Q0;
            {var subQ25=sQuery(id+"F0.wireOp",EDGE,"E0.top");Q0=makeQuery(id+"F0.imprint","IMPRINT",FACE,{"disambiguationData":[TD([[makeQuery(id+"F0.imprint","IMPRINT",EDGE,{"derivedFrom":subQ25}),1.0]])]});}
            var Q1;
            Q1=makeQuery(id+"F0.imprint","IMPRINT",FACE,{"disambiguationData":[TD([[makeQuery(id+"F0.imprint","IMPRINT",EDGE,{"derivedFrom":sQuery(id+"F0.wireOp",EDGE,"E2")}),1.0]])]});
            var Q2;
            {var subQ2=sQuery(id+"F0.wireOp",EDGE,"E14.MirrorCS");Q2=makeQuery(id+"F0.imprint","IMPRINT",FACE,{"disambiguationData":[TD([[makeQuery(id+"F0.imprint","IMPRINT",EDGE,{"derivedFrom":subQ2}),-1.0]])]});}
            var Q3;
            {var subQ0=sQuery(id+"F0.wireOp",EDGE,"E11.MirrorCS");Q3=makeQuery(id+"F0.imprint","IMPRINT",FACE,{"disambiguationData":[TD([[makeQuery(id+"F0.imprint","IMPRINT",EDGE,{"derivedFrom":subQ0}),-1.0]])]});}
            var Q4;
            {var subQ0=sQuery(id+"F0.wireOp",EDGE,"E5.left");var subQ1=sQuery(id+"F0.wireOp",EDGE,"E1");var subQ2=makeQuery(id+"F0.imprint","INTERSECT",VERTEX,{"derivedFrom":[subQ1,subQ0]});Q4=makeQuery(id+"F0.imprint","IMPRINT",FACE,{"disambiguationData":[TD([[makeQuery(id+"F0.imprint","IMPRINT",EDGE,{"disambiguationData":[TD([[subQ2,-1.0]])],"derivedFrom":subQ1}),1.0]])]});}
            var Q5;
            {var subQ0=sQuery(id+"F0.wireOp",EDGE,"E5.right");var subQ1=sQuery(id+"F0.wireOp",EDGE,"E1");var subQ2=makeQuery(id+"F0.imprint","INTERSECT",VERTEX,{"derivedFrom":[subQ1,subQ0]});Q5=makeQuery(id+"F0.imprint","IMPRINT",FACE,{"disambiguationData":[TD([[makeQuery(id+"F0.imprint","IMPRINT",EDGE,{"disambiguationData":[TD([[subQ2,1.0]])],"derivedFrom":subQ1}),1.0]])]});}
            var Q6;
            {var subQ0=sQuery(id+"F0.wireOp",EDGE,"E5.left");var subQ1=sQuery(id+"F0.wireOp",EDGE,"E1");var subQ2=makeQuery(id+"F0.imprint","INTERSECT",VERTEX,{"derivedFrom":[subQ1,subQ0]});Q6=makeQuery(id+"F0.imprint","IMPRINT",FACE,{"disambiguationData":[TD([[makeQuery(id+"F0.imprint","IMPRINT",EDGE,{"disambiguationData":[TD([[subQ2,-1.0]])],"derivedFrom":subQ1}),-1.0]])]});}
            var Q7;
            {var subQ0=sQuery(id+"F0.wireOp",EDGE,"E5.right");var subQ1=sQuery(id+"F0.wireOp",EDGE,"E1");var subQ2=makeQuery(id+"F0.imprint","INTERSECT",VERTEX,{"derivedFrom":[subQ1,subQ0]});Q7=makeQuery(id+"F0.imprint","IMPRINT",FACE,{"disambiguationData":[TD([[makeQuery(id+"F0.imprint","IMPRINT",EDGE,{"disambiguationData":[TD([[subQ2,1.0]])],"derivedFrom":subQ1}),-1.0]])]});}
            var Q8;
            Q8=makeQuery(id+"F0.imprint","IMPRINT",FACE,{"disambiguationData":[TD([[makeQuery(id+"F0.imprint","IMPRINT",EDGE,{"derivedFrom":sQuery(id+"F0.wireOp",EDGE,"E6.bottom")}),-1.0]])]});
            var Q9;
            Q9=makeQuery(id+"F0.imprint","IMPRINT",FACE,{"disambiguationData":[TD([[makeQuery(id+"F0.imprint","IMPRINT",EDGE,{"derivedFrom":sQuery(id+"F0.wireOp",EDGE,"E7.top")}),1.0]])]});
            var Q10;
            Q10=makeQuery(id+"F0.imprint","IMPRINT",FACE,{"disambiguationData":[TD([[makeQuery(id+"F0.imprint","IMPRINT",EDGE,{"derivedFrom":sQuery(id+"F0.wireOp",EDGE,"E10.bottom")}),1.0]])]});
            var Q11;
            Q11=makeQuery(id+"F0.imprint","IMPRINT",FACE,{"disambiguationData":[TD([[makeQuery(id+"F0.imprint","IMPRINT",EDGE,{"derivedFrom":sQuery(id+"F0.wireOp",EDGE,"E9.top")}),1.0]])]});
            var Q12;
            Q12=makeQuery(id+"F0.imprint","IMPRINT",FACE,{"disambiguationData":[TD([[makeQuery(id+"F0.imprint","IMPRINT",EDGE,{"derivedFrom":sQuery(id+"F0.wireOp",EDGE,"E21.bottom")}),1.0]])]});
            var Q13;
            {var subQ1=sQuery(id+"F0.wireOp",EDGE,"E20.top");Q13=makeQuery(id+"F0.imprint","IMPRINT",FACE,{"disambiguationData":[TD([[makeQuery(id+"F0.imprint","IMPRINT",EDGE,{"derivedFrom":subQ1}),-1.0]])]});}
            var Q14;
            {var subQ1=sQuery(id+"F0.wireOp",EDGE,"E19.top");Q14=makeQuery(id+"F0.imprint","IMPRINT",FACE,{"disambiguationData":[TD([[makeQuery(id+"F0.imprint","IMPRINT",EDGE,{"derivedFrom":subQ1}),-1.0]])]});}
            var Q15;
            {var subQ0=sQuery(id+"F0.wireOp",EDGE,"E19.bottom");Q15=makeQuery(id+"F0.imprint","IMPRINT",FACE,{"disambiguationData":[TD([[makeQuery(id+"F0.imprint","IMPRINT",EDGE,{"derivedFrom":subQ0}),1.0]])]});}
            var Q16;
            {var subQ0=sQuery(id+"F0.wireOp",EDGE,"E20.bottom");Q16=makeQuery(id+"F0.imprint","IMPRINT",FACE,{"disambiguationData":[TD([[makeQuery(id+"F0.imprint","IMPRINT",EDGE,{"derivedFrom":subQ0}),1.0]])]});}
            var Q17;
            Q17=makeQuery(id+"F0.imprint","IMPRINT",FACE,{"disambiguationData":[TD([[makeQuery(id+"F0.imprint","IMPRINT",EDGE,{"derivedFrom":sQuery(id+"F0.wireOp",EDGE,"E2")}),-1.0]])]});
            var Q18;
            Q18=makeQuery(id+"F0.imprint","IMPRINT",FACE,{"disambiguationData":[TD([[makeQuery(id+"F0.imprint","IMPRINT",EDGE,{"derivedFrom":sQuery(id+"F0.wireOp",EDGE,"E17.bottom")}),1.0]])]});
            extrude(context, id + "F10", {"entities" : qUnion([Q0, Q1, Q2, Q3, Q4, Q5, Q6, Q7, Q8, Q9, Q10, Q11, Q12, Q13, Q14, Q15, Q16, Q17, Q18]), "oppositeDirection" : true, "depth" : 100 * mm, "offsetDistance" : 25 * mm});
        }
        {
            var Q0;
            Q0=makeQuery(id+"F0.imprint","IMPRINT",FACE,{"disambiguationData":[TD([[makeQuery(id+"F0.imprint","IMPRINT",EDGE,{"derivedFrom":sQuery(id+"F0.wireOp",EDGE,"E2")}),1.0]])]});
            extrude(context, id + "F11", {"entities" : qUnion([Q0]), "operationType" : NewBodyOperationType.ADD, "depth" : 50 * mm, "offsetDistance" : 25 * mm});
        }
        {
            var Q0;
            Q0=makeQuery(id+"F1.opExtrude","CAP_FACE",FACE,{"disambiguationData":[OSD([sQuery(id+"F0.wireOp",EDGE,"E8.bottom"),sQuery(id+"F0.wireOp",EDGE,"E14.MirrorCS"),sQuery(id+"F0.wireOp",EDGE,"E15.MirrorCS"),sQuery(id+"F0.wireOp",EDGE,"E16.MirrorCS")])],"isStart":false});
            var sketch = newSketch(context, id + "F12", { "sketchPlane" : qUnion([Q0])});
            skCircle(sketch, "E102", {"center": v(-3512.12, 975.82) * mm, "radius": 35 * mm});
            skCircle(sketch, "E103", {"center": v(-287.66, 4227.4) * mm, "radius": 35 * mm});
            skSolve(sketch);
        }
        {
            var Q0;
            Q0=makeQuery(id+"F12.imprint","IMPRINT",FACE,{"disambiguationData":[TD([[makeQuery(id+"F12.imprint","IMPRINT",EDGE,{"derivedFrom":sQuery(id+"F12.wireOp",EDGE,"E102")}),1.0]])]});
            var Q1;
            Q1=makeQuery(id+"F12.imprint","IMPRINT",FACE,{"disambiguationData":[TD([[makeQuery(id+"F12.imprint","IMPRINT",EDGE,{"derivedFrom":sQuery(id+"F12.wireOp",EDGE,"E103")}),1.0]])]});
            extrude(context, id + "F13", {"entities" : qUnion([Q0, Q1]), "operationType" : NewBodyOperationType.ADD, "depth" : 370 * mm, "offsetDistance" : 25 * mm});
        }
        {
            var Q0;
            Q0=makeQuery(id+"F13.opExtrude","CAP_FACE",FACE,{"disambiguationData":[OSD([sQuery(id+"F12.wireOp",EDGE,"E103")])],"isStart":true});
            var sketch = newSketch(context, id + "F14", { "sketchPlane" : qUnion([Q0])});
            skCircle(sketch, "E104", {"center": v(-287.66, -4227.4) * mm, "radius": 10 * mm});
            skSolve(sketch);
        }
        {
            var Q0;
            Q0=makeQuery(id+"F14.imprint","IMPRINT",FACE,{"disambiguationData":[TD([[makeQuery(id+"F14.imprint","IMPRINT",EDGE,{"derivedFrom":sQuery(id+"F14.wireOp",EDGE,"E104")}),1.0]])]});
            extrude(context, id + "F15", {"entities" : qUnion([Q0]), "depth" : 350 * mm, "offsetDistance" : 25 * mm});
        }
        {
            var Q0;
            Q0=makeQuery(id+"F3.boolean.opBoolean","MERGE",FACE,{"derivedFrom":[makeQuery(id+"F2.opExtrude","SWEPT_FACE",FACE,{"disambiguationData":[OSD([sQuery(id+"F0.wireOp",EDGE,"E6.left")])]}),makeQuery(id+"F3.opExtrude","SWEPT_FACE",FACE,{"disambiguationData":[OSD([sQuery(id+"F0.wireOp",EDGE,"E7.left")])]})]});
            var sketch = newSketch(context, id + "F16", { "sketchPlane" : qUnion([Q0])});
            skLineSegment(sketch, "E105.bottom", {"start": v(3789.25, 1486.84) * mm, "end": v(2946.9, 1486.84) * mm});
            skLineSegment(sketch, "E105.top", {"start": v(3789.25, 722.05) * mm, "end": v(2946.9, 722.05) * mm});
            skLineSegment(sketch, "E105.left", {"start": v(3789.25, 1486.84) * mm, "end": v(3789.25, 722.05) * mm});
            skLineSegment(sketch, "E105.right", {"start": v(2946.9, 1486.84) * mm, "end": v(2946.9, 722.05) * mm});
            skSolve(sketch);
        }
        {
            var Q0;
            Q0 = qSketchRegion(id + "F16", true);
            extrude(context, id + "F17", {"entities" : qUnion([Q0]), "operationType" : NewBodyOperationType.REMOVE, "oppositeDirection" : true, "depth" : 500 * mm, "offsetDistance" : 25 * mm});
        }
    });
